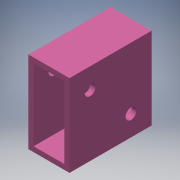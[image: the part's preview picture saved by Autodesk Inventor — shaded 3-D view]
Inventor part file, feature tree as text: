
AUTODESK INVENTOR PART (.ipt)
format: ipt  version: 2016 (Build 200138000, 138)  size: 110,080 bytes
history: native  units: in
note: dims shown in document units (in); Inventor stores cm internally (conversion verified against a paired STEP export)
features: extrude x2, sketch x2
ambient origin geometry x8: Origin, YZ Plane, XZ Plane, XY Plane, X Axis, Y Axis, Z Axis, Center Point
bodies: Solid1 (feature_tree)
feature tree (4):
  extrude  "Extrusion1"  Depth=2.0in
  extrude  "Extrusion2"  Depth=2.0in TaperAngle=0.0deg
  sketch  "Sketch1"  dims[d0=1.0in d1=2.0in]
  sketch  "Sketch2"  dims[d2=0.125in d3=2.0in d4=0.0in d5=0.2656in d6=0.2656in d7=0.5in d8=0.5in d9=0.5in d10=0.5in d11=1.0in d12=0.0in]
